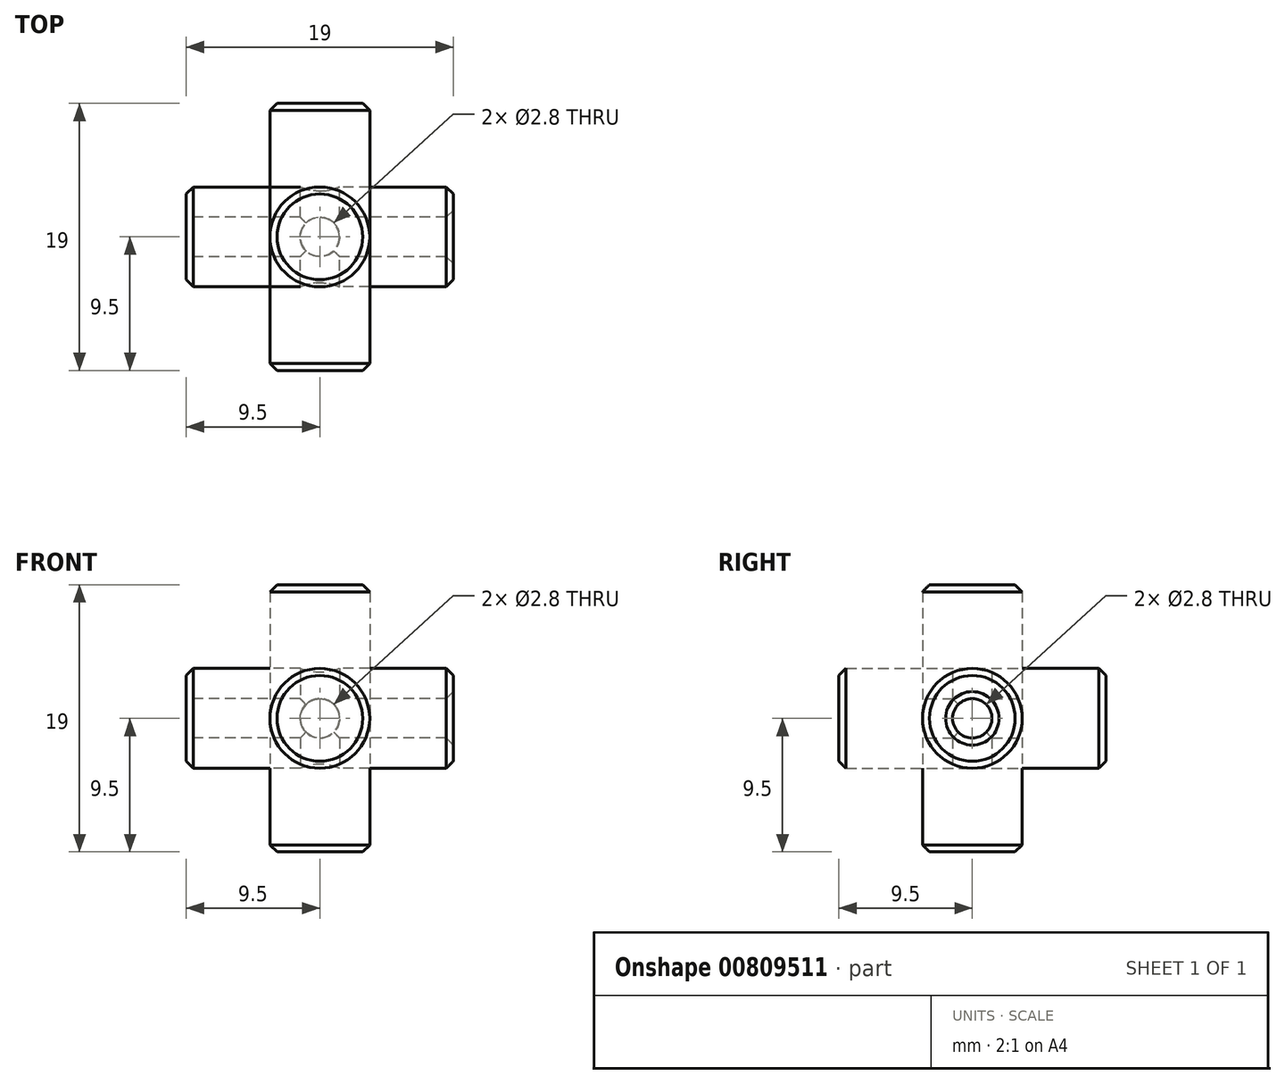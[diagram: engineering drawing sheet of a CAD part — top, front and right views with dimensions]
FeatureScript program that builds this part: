
annotation { "Feature Type Name" : "Feature", "Feature Type Description" : "" }
export const myFeature = defineFeature(function(context is Context, id is Id, definition is map)
    precondition{}
    {
        {
            var Q0;
            Q0=qCreatedBy(makeId("Front.planeOp"),FACE);
            var sketch = newSketch(context, id + "F0", { "sketchPlane" : qUnion([Q0])});
            skCircle(sketch, "E0", {"center": v(0, 0) * mm, "radius": 3.55 * mm});
            skSolve(sketch);
        }
        {
            var Q0;
            Q0 = qSketchRegion(id + "F0", true);
            extrude(context, id + "F1", {"entities" : qUnion([Q0]), "endBound" : BoundingType.SYMMETRIC, "depth" : 19 * mm, "offsetDistance" : 25 * mm});
        }
        {
            var Q0;
            Q0=qCreatedBy(makeId("Front.planeOp"),FACE);
            var sketch = newSketch(context, id + "F2", { "sketchPlane" : qUnion([Q0])});
            skCircle(sketch, "E1", {"center": v(0, 0) * mm, "radius": 1.4 * mm});
            skSolve(sketch);
        }
        {
            var Q0;
            Q0 = qSketchRegion(id + "F2", true);
            extrude(context, id + "F3", {"entities" : qUnion([Q0]), "endBound" : BoundingType.SYMMETRIC, "depth" : 20 * mm, "offsetDistance" : 25 * mm});
        }
        {
            var Q0;
            Q0=qCreatedBy(makeId("Front.planeOp"),FACE);
            var sketch = newSketch(context, id + "F4", { "sketchPlane" : qUnion([Q0])});
            skLineSegment(sketch, "E2.bottom", {"start": v(0, 0) * mm, "end": v(10, 0) * mm});
            skLineSegment(sketch, "E2.top", {"start": v(0, 10) * mm, "end": v(10, 10) * mm});
            skLineSegment(sketch, "E2.left", {"start": v(0, 0) * mm, "end": v(0, 10) * mm});
            skLineSegment(sketch, "E2.right", {"start": v(10, 0) * mm, "end": v(10, 10) * mm});
            skSolve(sketch);
        }
        {
            var Q0;
            Q0 = qSketchRegion(id + "F4", true);
            extrude(context, id + "F5", {"entities" : qUnion([Q0]), "depth" : 10 * mm, "offsetDistance" : 25 * mm});
        }
        {
            var Q0;
            Q0=qCreatedBy(makeId("Origin.pointOp"),VERTEX);
            var Q1;
            Q1=makeQuery(id+"F5.opExtrude","CAP_VERTEX",VERTEX,{"disambiguationData":[OSD([sQuery(id+"F4.wireOp",EDGE,"E2.top"),sQuery(id+"F4.wireOp",EDGE,"E2.right")])],"isStart":false});
            var Q2;
            Q2=makeQuery(id+"F5.opExtrude","CAP_VERTEX",VERTEX,{"disambiguationData":[OSD([sQuery(id+"F4.wireOp",EDGE,"E2.bottom"),sQuery(id+"F4.wireOp",EDGE,"E2.right")])],"isStart":false});
            cPlane(context, id + "F6", {"entities" : qUnion([Q0, Q1, Q2]), "cplaneType" : CPlaneType.THREE_POINT, "offset" : 25 * mm, "width" : 150 * mm, "height" : 150 * mm});
        }
        {
            var Q0;
            Q0=qCreatedBy(id+"F6.planeOp",FACE);
            var sketch = newSketch(context, id + "F7", { "sketchPlane" : qUnion([Q0])});
            skLineSegment(sketch, "E3", {"start": v(0, 0) * mm, "end": v(14.14, 10) * mm});
            skSolve(sketch);
        }
        {
            var Q0;
            Q0=makeQuery(id+"F5.opExtrude","SWEPT_BODY",BODY,{"disambiguationData":[OSD([sQuery(id+"F4.wireOp",EDGE,"E2.bottom"),sQuery(id+"F4.wireOp",EDGE,"E2.top"),sQuery(id+"F4.wireOp",EDGE,"E2.left"),sQuery(id+"F4.wireOp",EDGE,"E2.right")])]});
            deleteBodies(context, id + "F8", {"entities" : qUnion([Q0])});
        }
        {
            var Q0;
            Q0=makeQuery(id+"F3.opExtrude","SWEPT_BODY",BODY,{"disambiguationData":[OSD([sQuery(id+"F2.wireOp",EDGE,"E1")])]});
            var Q1;
            Q1=makeQuery(id+"F1.opExtrude","SWEPT_BODY",BODY,{"disambiguationData":[OSD([sQuery(id+"F0.wireOp",EDGE,"E0")])]});
            var Q2;
            Q2=sQuery(id+"F7.wireOp",EDGE,"E3");
            circularPattern(context, id + "F9", {"entities" : qUnion([Q0, Q1]), "axis" : qUnion([Q2]), "angle" : 360 * degree, "instanceCount" : 3, "equalSpace" : true});
        }
        {
            var Q0;
            Q0=makeQuery(id+"F9.opPattern","COPY",BODY,{"derivedFrom":makeQuery(id+"F3.opExtrude","SWEPT_BODY",BODY,{"disambiguationData":[OSD([sQuery(id+"F2.wireOp",EDGE,"E1")])]}),"instanceName":"2"});
            var Q1;
            Q1=makeQuery(id+"F3.opExtrude","SWEPT_BODY",BODY,{"disambiguationData":[OSD([sQuery(id+"F2.wireOp",EDGE,"E1")])]});
            var Q2;
            Q2=makeQuery(id+"F9.opPattern","COPY",BODY,{"derivedFrom":makeQuery(id+"F3.opExtrude","SWEPT_BODY",BODY,{"disambiguationData":[OSD([sQuery(id+"F2.wireOp",EDGE,"E1")])]}),"instanceName":"1"});
            var Q3;
            Q3=makeQuery(id+"F9.opPattern","COPY",BODY,{"derivedFrom":makeQuery(id+"F1.opExtrude","SWEPT_BODY",BODY,{"disambiguationData":[OSD([sQuery(id+"F0.wireOp",EDGE,"E0")])]}),"instanceName":"1"});
            booleanBodies(context, id + "F10", {"operationType" : BooleanOperationType.SUBTRACTION, "tools" : qUnion([Q0, Q1, Q2]), "targets" : qUnion([Q3])});
        }
        {
            var Q0;
            Q0=makeQuery(id+"F1.opExtrude","CAP_FACE",FACE,{"disambiguationData":[OSD([sQuery(id+"F0.wireOp",EDGE,"E0")])],"isStart":true});
            var Q1;
            Q1=makeQuery(id+"F9.opPattern","COPY",FACE,{"derivedFrom":makeQuery(id+"F1.opExtrude","CAP_FACE",FACE,{"disambiguationData":[OSD([sQuery(id+"F0.wireOp",EDGE,"E0")])],"isStart":false}),"instanceName":"2"});
            var Q2;
            Q2=makeQuery(id+"F9.opPattern","COPY",EDGE,{"derivedFrom":makeQuery(id+"F1.opExtrude","CAP_EDGE",EDGE,{"disambiguationData":[OSD([sQuery(id+"F0.wireOp",EDGE,"E0")])],"isStart":true}),"instanceName":"1"});
            var Q3;
            Q3=makeQuery(id+"F9.opPattern","COPY",FACE,{"derivedFrom":makeQuery(id+"F1.opExtrude","CAP_FACE",FACE,{"disambiguationData":[OSD([sQuery(id+"F0.wireOp",EDGE,"E0")])],"isStart":false}),"instanceName":"1"});
            var Q4;
            Q4=makeQuery(id+"F9.opPattern","COPY",FACE,{"derivedFrom":makeQuery(id+"F1.opExtrude","CAP_FACE",FACE,{"disambiguationData":[OSD([sQuery(id+"F0.wireOp",EDGE,"E0")])],"isStart":true}),"instanceName":"2"});
            var Q5;
            Q5=makeQuery(id+"F1.opExtrude","CAP_FACE",FACE,{"disambiguationData":[OSD([sQuery(id+"F0.wireOp",EDGE,"E0")])],"isStart":false});
            chamfer(context, id + "F11", {"entities" : qUnion([Q0, Q1, Q2, Q3, Q4, Q5]), "width" : 0.5 * mm, "tangentPropagation" : true});
        }
    });
